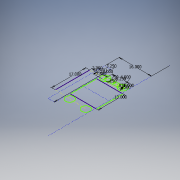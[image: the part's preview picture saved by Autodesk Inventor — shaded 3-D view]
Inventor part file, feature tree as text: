
AUTODESK INVENTOR PART (.ipt)
format: ipt  version: 2017 SP1 (Build 210196100, 196)  size: 109,568 bytes
history: native  units: in
note: dims shown in document units (in); Inventor stores cm internally (conversion verified against a paired STEP export)
features: sketch x1
ambient origin geometry x8: Origin, YZ Plane, XZ Plane, XY Plane, X Axis, Y Axis, Z Axis, Center Point
feature tree (1):
  sketch  "Sketch1"  dims[d0=28.0in d1=13.0in d2=3.25in d3=16.0in d4=4.0in d6=8.25in d7=2.0in d8=17.0in d9=0.875in d11=1.0in d12=0.5in d13=7.5in d14=0.75in d15=0.25in d16=1.875in]
